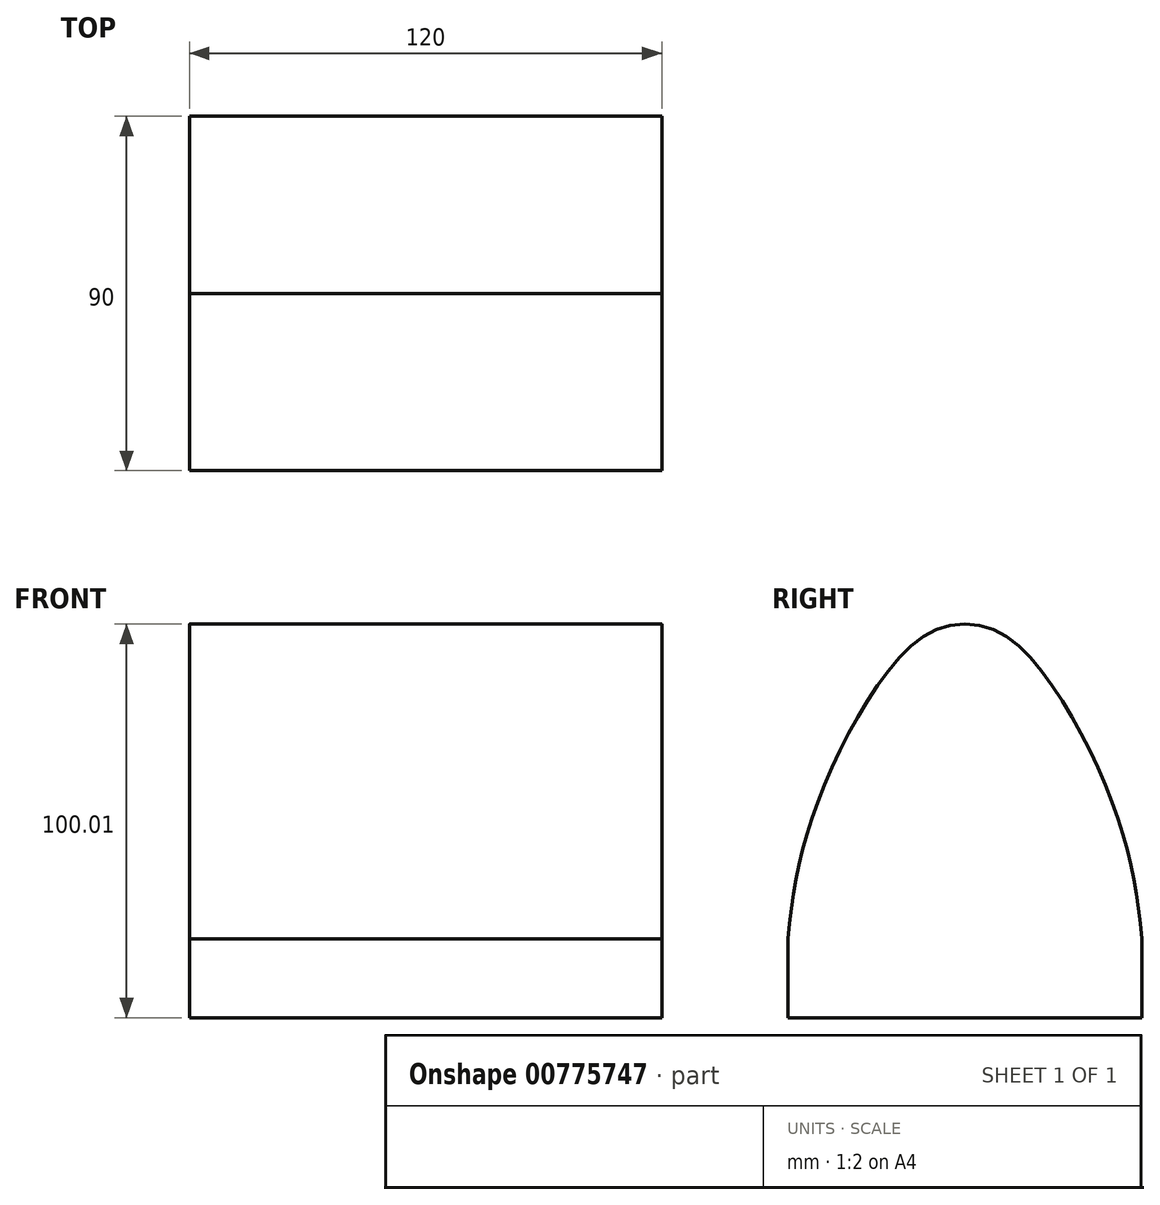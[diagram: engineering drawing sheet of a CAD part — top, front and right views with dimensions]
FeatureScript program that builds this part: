
annotation { "Feature Type Name" : "Feature", "Feature Type Description" : "" }
export const myFeature = defineFeature(function(context is Context, id is Id, definition is map)
    precondition{}
    {
        {
            var Q0;
            Q0=qCreatedBy(makeId("Top.planeOp"),FACE);
            var sketch = newSketch(context, id + "F0", { "sketchPlane" : qUnion([Q0])});
            skLineSegment(sketch, "E0.bottom", {"start": v(0, 45) * mm, "end": v(-120, 45) * mm});
            skLineSegment(sketch, "E0.top", {"start": v(0, -45) * mm, "end": v(-120, -45) * mm});
            skLineSegment(sketch, "E0.left", {"start": v(0, 45) * mm, "end": v(0, -45) * mm});
            skLineSegment(sketch, "E0.right", {"start": v(-120, 45) * mm, "end": v(-120, -45) * mm});
            skPoint(sketch, "E0.middle", {"position": v(-60, 0) * mm});
            skLineSegment(sketch, "E1.bottom", {"start": v(0, 35) * mm, "end": v(450, 35) * mm});
            skLineSegment(sketch, "E1.top", {"start": v(0, -35) * mm, "end": v(450, -35) * mm});
            skLineSegment(sketch, "E1.left", {"start": v(0, 35) * mm, "end": v(0, -35) * mm});
            skLineSegment(sketch, "E1.right", {"start": v(450, 35) * mm, "end": v(450, -35) * mm});
            skPoint(sketch, "E1.middle", {"position": v(225, 0) * mm});
            skSolve(sketch);
        }
        {
            var Q0;
            Q0=sQuery(id+"F0.wireOp",VERTEX,"E0.bottom.end");
            var Q1;
            Q1=qCreatedBy(makeId("Right.planeOp"),FACE);
            cPlane(context, id + "F1", {"entities" : qUnion([Q0, Q1]), "cplaneType" : CPlaneType.PLANE_POINT, "offset" : 0 * mm, "width" : 150 * mm, "height" : 150 * mm});
        }
        {
            var Q0;
            Q0=qCreatedBy(id+"F1.planeOp",FACE);
            var sketch = newSketch(context, id + "F2", { "sketchPlane" : qUnion([Q0])});
            skLineSegment(sketch, "E2.bottom", {"start": v(45, 0) * mm, "end": v(-45, 0) * mm});
            skLineSegment(sketch, "E2.top", {"start": v(45, 20) * mm, "end": v(-45, 20) * mm});
            skLineSegment(sketch, "E2.left", {"start": v(45, 0) * mm, "end": v(45, 20) * mm});
            skLineSegment(sketch, "E2.right", {"start": v(-45, 0) * mm, "end": v(-45, 20) * mm});
            skLineSegment(sketch, "E3", {"start": v(0, 0) * mm, "end": v(0, 100) * mm, "construction": true});
            skFitSpline(sketch, "E4", {"points": [v(45, 20) * mm, v(39.97, 47.2) * mm, v(22.65, 83.72) * mm, v(0, 100) * mm], "startDerivative": vector(-10.4, 92.41) * mm, "endDerivative": vector(-89.15, -2.84) * mm});
            skFitSpline(sketch, "E5.MirrorCS", {"points": [v(-45, 20) * mm, v(-39.97, 47.2) * mm, v(-22.65, 83.72) * mm, v(0, 100) * mm], "startDerivative": vector(10.4, 92.41) * mm, "endDerivative": vector(89.15, -2.84) * mm});
            skSolve(sketch);
        }
        {
            var Q0;
            Q0=makeQuery(id+"F2.imprint","IMPRINT",FACE,{"disambiguationData":[TD([[makeQuery(id+"F2.imprint","IMPRINT",EDGE,{"derivedFrom":sQuery(id+"F2.wireOp",EDGE,"E2.top")}),-1.0]])]});
            var Q1;
            Q1=makeQuery(id+"F2.imprint","IMPRINT",FACE,{"disambiguationData":[TD([[makeQuery(id+"F2.imprint","IMPRINT",EDGE,{"derivedFrom":sQuery(id+"F2.wireOp",EDGE,"E2.bottom")}),-1.0]])]});
            var Q2;
            Q2=sQuery(id+"F0.wireOp",VERTEX,"E0.top.start");
            extrude(context, id + "F3", {"entities" : qUnion([Q0, Q1]), "endBound" : BoundingType.UP_TO_VERTEX, "depth" : 25 * mm, "endBoundEntityVertex" : qUnion([Q2]), "offsetDistance" : 25 * mm});
        }
    });
